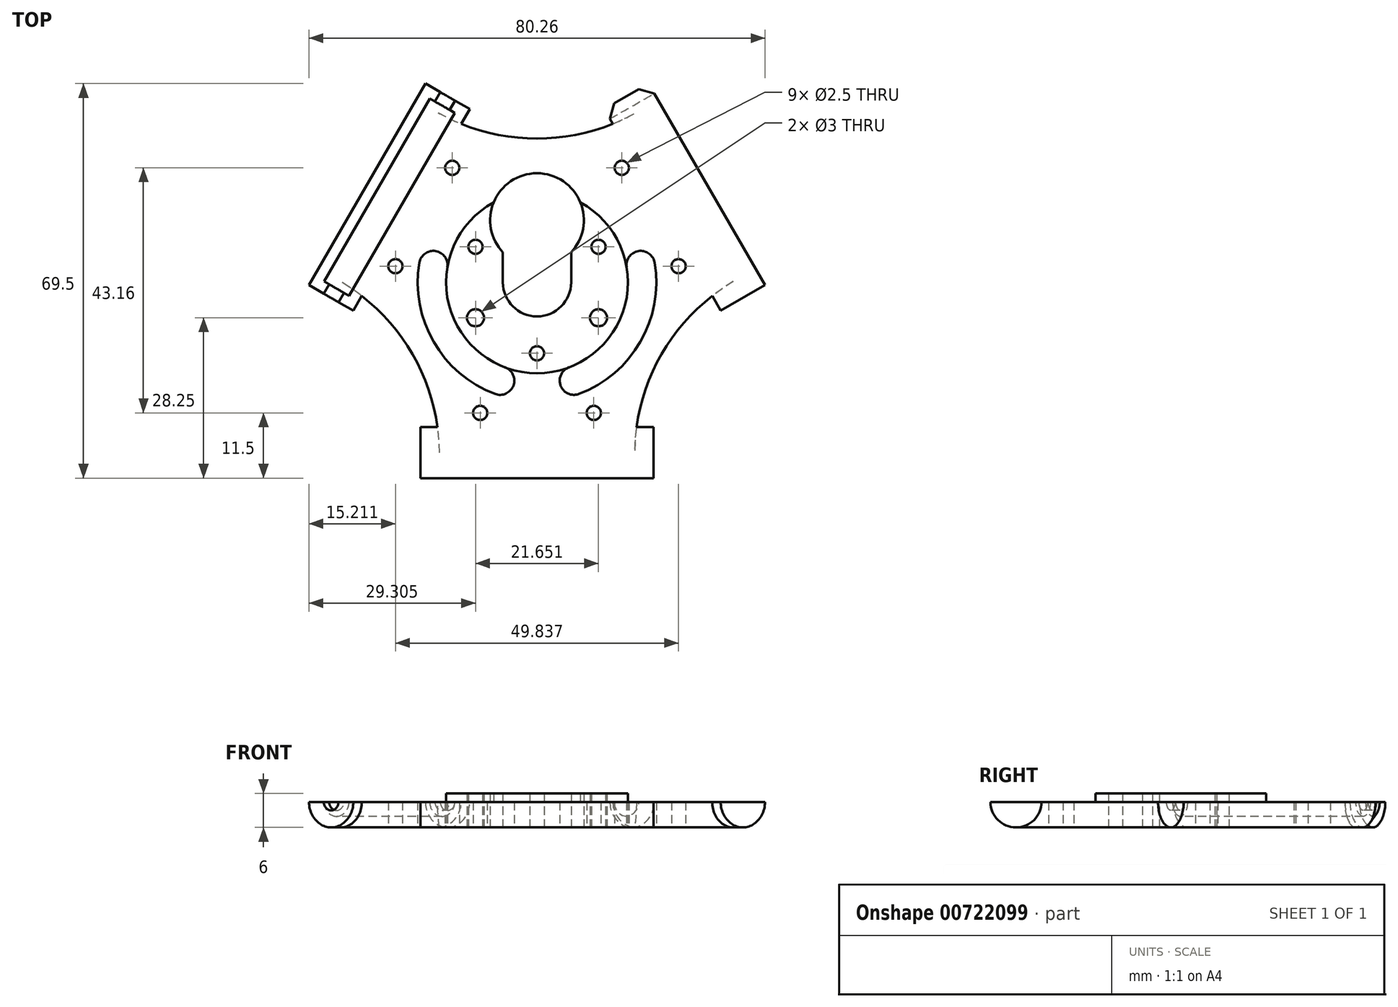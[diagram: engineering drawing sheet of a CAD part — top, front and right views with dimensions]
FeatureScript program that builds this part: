
annotation { "Feature Type Name" : "Feature", "Feature Type Description" : "" }
export const myFeature = defineFeature(function(context is Context, id is Id, definition is map)
    precondition{}
    {
        {
            var Q0;
            Q0=qCreatedBy(makeId("Top.planeOp"),FACE);
            var sketch = newSketch(context, id + "F0", { "sketchPlane" : qUnion([Q0])});
            skArc(sketch, "E0", {"start": v(-6, 0) * mm, "mid": v(0, -6) * mm, "end": v(6, 0) * mm});
            skArc(sketch, "E1", {"start": v(6, 5.3) * mm, "mid": v(0, 19.2) * mm, "end": v(-6, 5.3) * mm});
            skLineSegment(sketch, "E2", {"start": v(6, 0) * mm, "end": v(6, 5.3) * mm});
            skLineSegment(sketch, "E3", {"start": v(-6, 0) * mm, "end": v(-6, 5.3) * mm});
            skLineSegment(sketch, "E4", {"start": v(-32.33, -5) * mm, "end": v(-30.83, -2.4) * mm});
            skLineSegment(sketch, "E5", {"start": v(-11.83, 30.5) * mm, "end": v(-19.63, 35) * mm});
            skLineSegment(sketch, "E6", {"start": v(-19.63, 35) * mm, "end": v(-40.13, -0.5) * mm});
            skLineSegment(sketch, "E7", {"start": v(-40.13, -0.5) * mm, "end": v(-32.33, -5) * mm});
            skLineSegment(sketch, "E8", {"start": v(-36.23, -2.75) * mm, "end": v(-15.73, 32.75) * mm, "construction": true});
            skLineSegment(sketch, "E9", {"start": v(-25.98, 15) * mm, "end": v(0, 0) * mm, "construction": true});
            skCircle(sketch, "E10", {"center": v(0, 0) * mm, "radius": 8 * mm, "construction": true});
            skLineSegment(sketch, "E11.1.0", {"start": v(20.5, -25.5) * mm, "end": v(17.5, -25.5) * mm});
            skLineSegment(sketch, "E11.1.1", {"start": v(-20.5, -25.5) * mm, "end": v(-20.5, -34.5) * mm});
            skLineSegment(sketch, "E11.1.2", {"start": v(-20.5, -34.5) * mm, "end": v(20.5, -34.5) * mm});
            skLineSegment(sketch, "E11.1.3", {"start": v(20.5, -34.5) * mm, "end": v(20.5, -25.5) * mm});
            skLineSegment(sketch, "E11.1.4", {"start": v(0, -30) * mm, "end": v(0, 0) * mm, "construction": true});
            skLineSegment(sketch, "E11.1.5", {"start": v(20.5, -30) * mm, "end": v(-20.5, -30) * mm, "construction": true});
            skLineSegment(sketch, "E11.2.0", {"start": v(11.83, 30.5) * mm, "end": v(13.33, 27.9) * mm});
            skLineSegment(sketch, "E11.2.1", {"start": v(32.33, -5) * mm, "end": v(40.13, -0.5) * mm});
            skLineSegment(sketch, "E11.2.2", {"start": v(40.13, -0.5) * mm, "end": v(19.63, 35) * mm});
            skLineSegment(sketch, "E11.2.3", {"start": v(19.63, 35) * mm, "end": v(11.83, 30.5) * mm});
            skLineSegment(sketch, "E11.2.4", {"start": v(25.98, 15) * mm, "end": v(0, 0) * mm, "construction": true});
            skLineSegment(sketch, "E11.2.5", {"start": v(15.73, 32.75) * mm, "end": v(36.23, -2.75) * mm, "construction": true});
            skArc(sketch, "E12", {"start": v(-13.33, 27.9) * mm, "mid": v(0, 25.3) * mm, "end": v(13.33, 27.9) * mm});
            skArc(sketch, "E13.1.0", {"start": v(-17.5, -25.5) * mm, "mid": v(-21.92, -12.65) * mm, "end": v(-30.83, -2.4) * mm});
            skArc(sketch, "E13.2.0", {"start": v(30.83, -2.4) * mm, "mid": v(21.92, -12.65) * mm, "end": v(17.5, -25.5) * mm});
            skLineSegment(sketch, "E14.trimOffspring", {"start": v(-13.33, 27.9) * mm, "end": v(-11.83, 30.5) * mm});
            skLineSegment(sketch, "E15.trimOffspring", {"start": v(-17.5, -25.5) * mm, "end": v(-20.5, -25.5) * mm});
            skLineSegment(sketch, "E16.trimOffspring", {"start": v(30.83, -2.4) * mm, "end": v(32.33, -5) * mm});
            skCircle(sketch, "E17", {"center": v(0, -12.5) * mm, "radius": 1.25 * mm});
            skCircle(sketch, "E18.2.0", {"center": v(10.83, 6.25) * mm, "radius": 1.25 * mm});
            skCircle(sketch, "E18.4.0", {"center": v(-10.83, 6.25) * mm, "radius": 1.25 * mm});
            skCircle(sketch, "E18.5.0", {"center": v(-10.83, -6.25) * mm, "radius": 1.5 * mm});
            skCircle(sketch, "E19", {"center": v(-24.92, 2.84) * mm, "radius": 1.25 * mm});
            skCircle(sketch, "E20.MirrorC", {"center": v(-14.92, 20.16) * mm, "radius": 1.25 * mm});
            skArc(sketch, "E21", {"start": v(-15.78, 2.62) * mm, "mid": v(-13.86, -8) * mm, "end": v(-5.62, -14.98) * mm});
            skCircle(sketch, "E22.1.0", {"center": v(10, -23) * mm, "radius": 1.25 * mm});
            skCircle(sketch, "E22.1.1", {"center": v(-10, -23) * mm, "radius": 1.25 * mm});
            skCircle(sketch, "E22.2.0", {"center": v(14.92, 20.16) * mm, "radius": 1.25 * mm});
            skCircle(sketch, "E22.2.1", {"center": v(24.92, 2.84) * mm, "radius": 1.25 * mm});
            skArc(sketch, "E23", {"start": v(-20.72, 3.44) * mm, "mid": v(-18.19, -10.5) * mm, "end": v(-7.38, -19.66) * mm});
            skArc(sketch, "E24", {"start": v(-15.78, 2.62) * mm, "mid": v(-17.84, 5.5) * mm, "end": v(-20.72, 3.44) * mm});
            skArc(sketch, "E25", {"start": v(-7.38, -19.66) * mm, "mid": v(-4.16, -18.2) * mm, "end": v(-5.62, -14.98) * mm});
            skArc(sketch, "E26.MirrorCS", {"start": v(15.78, 2.62) * mm, "mid": v(13.86, -8) * mm, "end": v(5.62, -14.98) * mm});
            skArc(sketch, "E27.MirrorCS", {"start": v(20.72, 3.44) * mm, "mid": v(18.19, -10.5) * mm, "end": v(7.38, -19.66) * mm});
            skArc(sketch, "E28.MirrorCS", {"start": v(15.78, 2.62) * mm, "mid": v(17.84, 5.5) * mm, "end": v(20.72, 3.44) * mm});
            skArc(sketch, "E29.MirrorCS", {"start": v(7.38, -19.66) * mm, "mid": v(4.16, -18.2) * mm, "end": v(5.62, -14.98) * mm});
            skLineSegment(sketch, "E30", {"start": v(-10.83, -6.25) * mm, "end": v(0, 0) * mm, "construction": true});
            skCircle(sketch, "E31", {"center": v(0, 0) * mm, "radius": 12.5 * mm, "construction": true});
            skCircle(sketch, "E32.MirrorC", {"center": v(10.83, -6.25) * mm, "radius": 1.5 * mm});
            skSolve(sketch);
        }
        {
            var Q0;
            Q0=qSketchRegion(id+"F0",true);
            extrude(context, id + "F1", {"entities" : qUnion([Q0]), "depth" : 4.5 * mm, "offsetDistance" : 25 * mm});
        }
        {
            var Q0;
            Q0=makeQuery(id+"F1.opExtrude","SWEPT_FACE",FACE,{"disambiguationData":[OSD([sQuery(id+"F0.wireOp",EDGE,"E7")])]});
            var sketch = newSketch(context, id + "F2", { "sketchPlane" : qUnion([Q0])});
            skCircle(sketch, "E33", {"center": v(-30, 4.5) * mm, "radius": 1.5 * mm});
            skSolve(sketch);
        }
        {
            var Q0;
            Q0=qSketchRegion(id+"F2",true);
            extrude(context, id + "F3", {"entities" : qUnion([Q0]), "operationType" : NewBodyOperationType.REMOVE, "endBound" : BoundingType.THROUGH_ALL, "oppositeDirection" : true, "depth" : 25 * mm, "offsetDistance" : 25 * mm});
        }
        {
            var Q0;
            Q0=makeQuery(id+"F1.opExtrude","SWEPT_FACE",FACE,{"disambiguationData":[OSD([sQuery(id+"F0.wireOp",EDGE,"E7")])]});
            var Q1;
            Q1=qCreatedBy(makeId("Origin.pointOp"),VERTEX);
            cPlane(context, id + "F4", {"entities" : qUnion([Q0, Q1]), "cplaneType" : CPlaneType.PLANE_POINT, "offset" : 25 * mm, "width" : 150 * mm, "height" : 150 * mm});
        }
        {
            var Q0;
            Q0=qCreatedBy(id+"F4.planeOp",FACE);
            var sketch = newSketch(context, id + "F5", { "sketchPlane" : qUnion([Q0])});
            skArc(sketch, "E34", {"start": v(-31.5, 4.5) * mm, "mid": v(-30, 3) * mm, "end": v(-28.5, 4.5) * mm, "construction": true});
            skCircle(sketch, "E35", {"center": v(-30, 4.5) * mm, "radius": 2.55 * mm});
            skSolve(sketch);
        }
        {
            var Q0;
            Q0=qSketchRegion(id+"F5",true);
            extrude(context, id + "F6", {"entities" : qUnion([Q0]), "operationType" : NewBodyOperationType.REMOVE, "oppositeDirection" : true, "depth" : (37.2 / 2) * mm, "offsetDistance" : 25 * mm, "hasSecondDirection" : true, "secondDirectionOppositeDirection" : false, "secondDirectionDepth" : (37.2 / 2) * mm});
        }
        {
            var Q0;
            Q0=qCreatedBy(makeId("Front.planeOp"),FACE);
            var sketch = newSketch(context, id + "F7", { "sketchPlane" : qUnion([Q0])});
            skLineSegment(sketch, "E36", {"start": v(0, 0) * mm, "end": v(0, 59.84) * mm, "construction": true});
            skSolve(sketch);
        }
        {
            var Q0;
            Q0=makeQuery(id+"F1.opExtrude","CAP_EDGE",EDGE,{"disambiguationData":[OSD([sQuery(id+"F0.wireOp",EDGE,"E4")])],"isStart":true});
            var Q1;
            Q1=makeQuery(id+"F1.opExtrude","CAP_EDGE",EDGE,{"disambiguationData":[OSD([sQuery(id+"F0.wireOp",EDGE,"E6")])],"isStart":true});
            var Q2;
            Q2=makeQuery(id+"F1.opExtrude","CAP_EDGE",EDGE,{"disambiguationData":[OSD([sQuery(id+"F0.wireOp",EDGE,"E14.trimOffspring")])],"isStart":true});
            var Q3;
            Q3=makeQuery(id+"F1.opExtrude","CAP_EDGE",EDGE,{"disambiguationData":[OSD([sQuery(id+"F0.wireOp",EDGE,"E15.trimOffspring")])],"isStart":true});
            var Q4;
            Q4=makeQuery(id+"F1.opExtrude","CAP_EDGE",EDGE,{"disambiguationData":[OSD([sQuery(id+"F0.wireOp",EDGE,"E11.1.2")])],"isStart":true});
            var Q5;
            Q5=makeQuery(id+"F1.opExtrude","CAP_EDGE",EDGE,{"disambiguationData":[OSD([sQuery(id+"F0.wireOp",EDGE,"E11.1.0")])],"isStart":true});
            var Q6;
            Q6=makeQuery(id+"F1.opExtrude","CAP_EDGE",EDGE,{"disambiguationData":[OSD([sQuery(id+"F0.wireOp",EDGE,"E16.trimOffspring")])],"isStart":true});
            var Q7;
            Q7=makeQuery(id+"F1.opExtrude","CAP_EDGE",EDGE,{"disambiguationData":[OSD([sQuery(id+"F0.wireOp",EDGE,"E11.2.2")])],"isStart":true});
            var Q8;
            Q8=makeQuery(id+"F1.opExtrude","CAP_EDGE",EDGE,{"disambiguationData":[OSD([sQuery(id+"F0.wireOp",EDGE,"E11.2.0")])],"isStart":true});
            fillet(context, id + "F8", {"entities" : qUnion([Q0, Q1, Q2, Q3, Q4, Q5, Q6, Q7, Q8]), "radius" : 4.5 * mm, "tangentPropagation" : true, "allowEdgeOverflow" : false});
        }
        {
            var Q0;
            Q0=makeQuery(id+"F8.opFillet","BLEND_EDGE",EDGE,{"blendedFrom":[makeQuery(id+"F1.opExtrude","CAP_EDGE",EDGE,{"disambiguationData":[OSD([sQuery(id+"F0.wireOp",EDGE,"E6")])],"isStart":true}),makeQuery(id+"F1.opExtrude","SWEPT_FACE",FACE,{"disambiguationData":[OSD([sQuery(id+"F0.wireOp",EDGE,"E7")])]})],"blendedInto":[makeQuery(id+"F1.opExtrude","SWEPT_FACE",FACE,{"disambiguationData":[OSD([sQuery(id+"F0.wireOp",EDGE,"E7")])]})]});
            var Q1;
            Q1=makeQuery(id+"F8.opFillet","BLEND_EDGE",EDGE,{"blendedFrom":[makeQuery(id+"F1.opExtrude","CAP_EDGE",EDGE,{"disambiguationData":[OSD([sQuery(id+"F0.wireOp",EDGE,"E14.trimOffspring")])],"isStart":true}),makeQuery(id+"F1.opExtrude","SWEPT_FACE",FACE,{"disambiguationData":[OSD([sQuery(id+"F0.wireOp",EDGE,"E5")])]})],"blendedInto":[makeQuery(id+"F1.opExtrude","SWEPT_FACE",FACE,{"disambiguationData":[OSD([sQuery(id+"F0.wireOp",EDGE,"E5")])]})]});
            var Q2;
            Q2=makeQuery(id+"F8.opFillet","BLEND_EDGE",EDGE,{"blendedFrom":[makeQuery(id+"F1.opExtrude","CAP_EDGE",EDGE,{"disambiguationData":[OSD([sQuery(id+"F0.wireOp",EDGE,"E11.2.0")])],"isStart":true}),makeQuery(id+"F1.opExtrude","SWEPT_FACE",FACE,{"disambiguationData":[OSD([sQuery(id+"F0.wireOp",EDGE,"E11.2.3")])]})],"blendedInto":[makeQuery(id+"F1.opExtrude","SWEPT_FACE",FACE,{"disambiguationData":[OSD([sQuery(id+"F0.wireOp",EDGE,"E11.2.3")])]})]});
            var Q3;
            Q3=makeQuery(id+"F8.opFillet","BLEND_EDGE",EDGE,{"blendedFrom":[makeQuery(id+"F1.opExtrude","CAP_EDGE",EDGE,{"disambiguationData":[OSD([sQuery(id+"F0.wireOp",EDGE,"E15.trimOffspring")])],"isStart":true}),makeQuery(id+"F1.opExtrude","SWEPT_FACE",FACE,{"disambiguationData":[OSD([sQuery(id+"F0.wireOp",EDGE,"E11.1.1")])]})],"blendedInto":[makeQuery(id+"F1.opExtrude","SWEPT_FACE",FACE,{"disambiguationData":[OSD([sQuery(id+"F0.wireOp",EDGE,"E11.1.1")])]})]});
            var Q4;
            Q4=makeQuery(id+"F8.opFillet","BLEND_EDGE",EDGE,{"blendedFrom":[makeQuery(id+"F1.opExtrude","CAP_EDGE",EDGE,{"disambiguationData":[OSD([sQuery(id+"F0.wireOp",EDGE,"E11.1.2")])],"isStart":true}),makeQuery(id+"F1.opExtrude","SWEPT_FACE",FACE,{"disambiguationData":[OSD([sQuery(id+"F0.wireOp",EDGE,"E11.1.3")])]})],"blendedInto":[makeQuery(id+"F1.opExtrude","SWEPT_FACE",FACE,{"disambiguationData":[OSD([sQuery(id+"F0.wireOp",EDGE,"E11.1.3")])]})]});
            var Q5;
            Q5=makeQuery(id+"F8.opFillet","BLEND_EDGE",EDGE,{"blendedFrom":[makeQuery(id+"F1.opExtrude","CAP_EDGE",EDGE,{"disambiguationData":[OSD([sQuery(id+"F0.wireOp",EDGE,"E16.trimOffspring")])],"isStart":true}),makeQuery(id+"F1.opExtrude","SWEPT_FACE",FACE,{"disambiguationData":[OSD([sQuery(id+"F0.wireOp",EDGE,"E11.2.1")])]})],"blendedInto":[makeQuery(id+"F1.opExtrude","SWEPT_FACE",FACE,{"disambiguationData":[OSD([sQuery(id+"F0.wireOp",EDGE,"E11.2.1")])]})]});
            chamfer(context, id + "F9", {"entities" : qUnion([Q0, Q1, Q2, Q3, Q4, Q5]), "width" : 2 * mm, "tangentPropagation" : true});
        }
        {
            var Q0;
            {var subQ0=sQuery(id+"F0.wireOp",EDGE,"E29.MirrorCS");var subQ2=sQuery(id+"F0.wireOp",EDGE,"E28.MirrorCS");var subQ4=sQuery(id+"F0.wireOp",EDGE,"E27.MirrorCS");var subQ8=sQuery(id+"F0.wireOp",EDGE,"E26.MirrorCS");var subQ11=sQuery(id+"F0.wireOp",EDGE,"E25");var subQ14=sQuery(id+"F0.wireOp",EDGE,"E24");var subQ16=sQuery(id+"F0.wireOp",EDGE,"E23");var subQ18=sQuery(id+"F0.wireOp",EDGE,"E22.2.1");var subQ20=sQuery(id+"F0.wireOp",EDGE,"E22.2.0");var subQ22=sQuery(id+"F0.wireOp",EDGE,"E22.1.1");var subQ24=sQuery(id+"F0.wireOp",EDGE,"E22.1.0");var subQ26=sQuery(id+"F0.wireOp",EDGE,"E21");var subQ28=sQuery(id+"F0.wireOp",EDGE,"E20.MirrorC");var subQ30=sQuery(id+"F0.wireOp",EDGE,"E19");var subQ32=sQuery(id+"F0.wireOp",EDGE,"E18.5.0");var subQ34=sQuery(id+"F0.wireOp",EDGE,"E18.4.0");var subQ36=sQuery(id+"F0.wireOp",EDGE,"E11.1.3");var subQ38=sQuery(id+"F0.wireOp",EDGE,"E11.1.0");var subQ40=sQuery(id+"F0.wireOp",EDGE,"E7");var subQ42=sQuery(id+"F0.wireOp",EDGE,"E5");var subQ47=sQuery(id+"F0.wireOp",EDGE,"E17");var subQ49=sQuery(id+"F0.wireOp",EDGE,"E4");var subQ51=sQuery(id+"F0.wireOp",EDGE,"E11.1.1");var subQ53=sQuery(id+"F0.wireOp",EDGE,"E0");var subQ54=makeQuery(id+"F1.opExtrude","SWEPT_FACE",FACE,{"disambiguationData":[OSD([subQ53])]});var subQ55=sQuery(id+"F0.wireOp",EDGE,"E16.trimOffspring");var subQ57=sQuery(id+"F0.wireOp",EDGE,"E3");var subQ59=sQuery(id+"F0.wireOp",EDGE,"E1");var subQ61=sQuery(id+"F0.wireOp",EDGE,"E18.2.0");var subQ63=sQuery(id+"F0.wireOp",EDGE,"E2");var subQ65=sQuery(id+"F0.wireOp",EDGE,"E11.2.0");var subQ67=sQuery(id+"F0.wireOp",EDGE,"E11.2.1");var subQ69=sQuery(id+"F0.wireOp",EDGE,"E11.2.3");var subQ72=sQuery(id+"F0.wireOp",EDGE,"E12");var subQ74=sQuery(id+"F0.wireOp",EDGE,"E13.1.0");var subQ76=sQuery(id+"F0.wireOp",EDGE,"E13.2.0");var subQ78=sQuery(id+"F0.wireOp",EDGE,"E14.trimOffspring");var subQ80=sQuery(id+"F0.wireOp",EDGE,"E15.trimOffspring");var subQ82=sQuery(id+"F0.wireOp",EDGE,"E18.1.0");var subQ84=sQuery(id+"F0.wireOp",EDGE,"E11.2.2");var subQ86=sQuery(id+"F0.wireOp",EDGE,"E11.1.2");Q0=makeQuery(id+"Fxi4iVRiwFdOaLl_1.2.F3.boolean.opBoolean","SPLIT",FACE,{"disambiguationData":[TD([subQ54])],"derivedFrom":makeQuery(id+"Fxi4iVRiwFdOaLl_1.1.F3.boolean.opBoolean","SPLIT",FACE,{"disambiguationData":[TD([subQ54])],"derivedFrom":makeQuery(id+"F3.boolean.opBoolean","SPLIT",FACE,{"disambiguationData":[TD([subQ54])],"derivedFrom":makeQuery(id+"F1.opExtrude","CAP_FACE",FACE,{"disambiguationData":[OSD([subQ53,subQ59,subQ63,subQ57,subQ49,subQ42,sQuery(id+"F0.wireOp",EDGE,"E6"),subQ40,subQ38,subQ51,subQ86,subQ36,subQ65,subQ67,subQ84,subQ69,subQ72,subQ74,subQ76,subQ78,subQ80,subQ55,subQ47,subQ82,subQ61,subQ34,subQ32,subQ30,subQ28,subQ26,subQ24,subQ22,subQ20,subQ18,subQ16,subQ14,subQ11,subQ8,subQ4,subQ2,subQ0])],"isStart":false})})})});}
            var sketch = newSketch(context, id + "F10", { "sketchPlane" : qUnion([Q0])});
            skArc(sketch, "E37", {"start": v(-7.64, 14.06) * mm, "mid": v(0, -16) * mm, "end": v(7.64, 14.06) * mm});
            skArc(sketch, "E38.0", {"start": v(6, 5.3) * mm, "mid": v(8.1, 9.43) * mm, "end": v(7.64, 14.06) * mm});
            skLineSegment(sketch, "E39.0", {"start": v(-6, 0) * mm, "end": v(-6, 5.3) * mm});
            skArc(sketch, "E40.0", {"start": v(-6, 0) * mm, "mid": v(0, -6) * mm, "end": v(6, 0) * mm});
            skLineSegment(sketch, "E41.0", {"start": v(6, 0) * mm, "end": v(6, 5.3) * mm});
            skCircle(sketch, "E42.0", {"center": v(10.83, 6.25) * mm, "radius": 1.25 * mm});
            skCircle(sketch, "E43.0", {"center": v(0, -12.5) * mm, "radius": 1.25 * mm});
            skCircle(sketch, "E44.0", {"center": v(-10.83, -6.25) * mm, "radius": 1.5 * mm});
            skCircle(sketch, "E45.0", {"center": v(-10.83, 6.25) * mm, "radius": 1.25 * mm});
            skArc(sketch, "E46.trimOffspring", {"start": v(-7.64, 14.06) * mm, "mid": v(-8.1, 9.43) * mm, "end": v(-6, 5.3) * mm});
            skCircle(sketch, "E47.0", {"center": v(10.83, -6.25) * mm, "radius": 1.5 * mm});
            skSolve(sketch);
        }
        {
            var Q0;
            Q0=qSketchRegion(id+"F10",true);
            var Q1;
            Q1=makeQuery(id+"F1.opExtrude","CAP_FACE",FACE,{"disambiguationData":[OSD([sQuery(id+"F0.wireOp",EDGE,"E0"),sQuery(id+"F0.wireOp",EDGE,"E1"),sQuery(id+"F0.wireOp",EDGE,"E2"),sQuery(id+"F0.wireOp",EDGE,"E3"),sQuery(id+"F0.wireOp",EDGE,"E4"),sQuery(id+"F0.wireOp",EDGE,"E5"),sQuery(id+"F0.wireOp",EDGE,"E6"),sQuery(id+"F0.wireOp",EDGE,"E7"),sQuery(id+"F0.wireOp",EDGE,"E11.1.0"),sQuery(id+"F0.wireOp",EDGE,"E11.1.1"),sQuery(id+"F0.wireOp",EDGE,"E11.1.2"),sQuery(id+"F0.wireOp",EDGE,"E11.1.3"),sQuery(id+"F0.wireOp",EDGE,"E11.2.0"),sQuery(id+"F0.wireOp",EDGE,"E11.2.1"),sQuery(id+"F0.wireOp",EDGE,"E11.2.2"),sQuery(id+"F0.wireOp",EDGE,"E11.2.3"),sQuery(id+"F0.wireOp",EDGE,"E12"),sQuery(id+"F0.wireOp",EDGE,"E13.1.0"),sQuery(id+"F0.wireOp",EDGE,"E13.2.0"),sQuery(id+"F0.wireOp",EDGE,"E14.trimOffspring"),sQuery(id+"F0.wireOp",EDGE,"E15.trimOffspring"),sQuery(id+"F0.wireOp",EDGE,"E16.trimOffspring"),sQuery(id+"F0.wireOp",EDGE,"E17"),sQuery(id+"F0.wireOp",EDGE,"E18.1.0"),sQuery(id+"F0.wireOp",EDGE,"E18.2.0"),sQuery(id+"F0.wireOp",EDGE,"E18.4.0"),sQuery(id+"F0.wireOp",EDGE,"E18.5.0"),sQuery(id+"F0.wireOp",EDGE,"E19"),sQuery(id+"F0.wireOp",EDGE,"E20.MirrorC"),sQuery(id+"F0.wireOp",EDGE,"E21"),sQuery(id+"F0.wireOp",EDGE,"E22.1.0"),sQuery(id+"F0.wireOp",EDGE,"E22.1.1"),sQuery(id+"F0.wireOp",EDGE,"E22.2.0"),sQuery(id+"F0.wireOp",EDGE,"E22.2.1"),sQuery(id+"F0.wireOp",EDGE,"E23"),sQuery(id+"F0.wireOp",EDGE,"E24"),sQuery(id+"F0.wireOp",EDGE,"E25"),sQuery(id+"F0.wireOp",EDGE,"E26.MirrorCS"),sQuery(id+"F0.wireOp",EDGE,"E27.MirrorCS"),sQuery(id+"F0.wireOp",EDGE,"E28.MirrorCS"),sQuery(id+"F0.wireOp",EDGE,"E29.MirrorCS")])],"isStart":true});
            extrude(context, id + "F11", {"entities" : qUnion([Q0]), "operationType" : NewBodyOperationType.ADD, "depth" : 1.5 * mm, "endBoundEntityFace" : qUnion([Q1]), "hasOffset" : true, "offsetDistance" : 10 * mm, "offsetOppositeDirection" : true});
        }
    });
